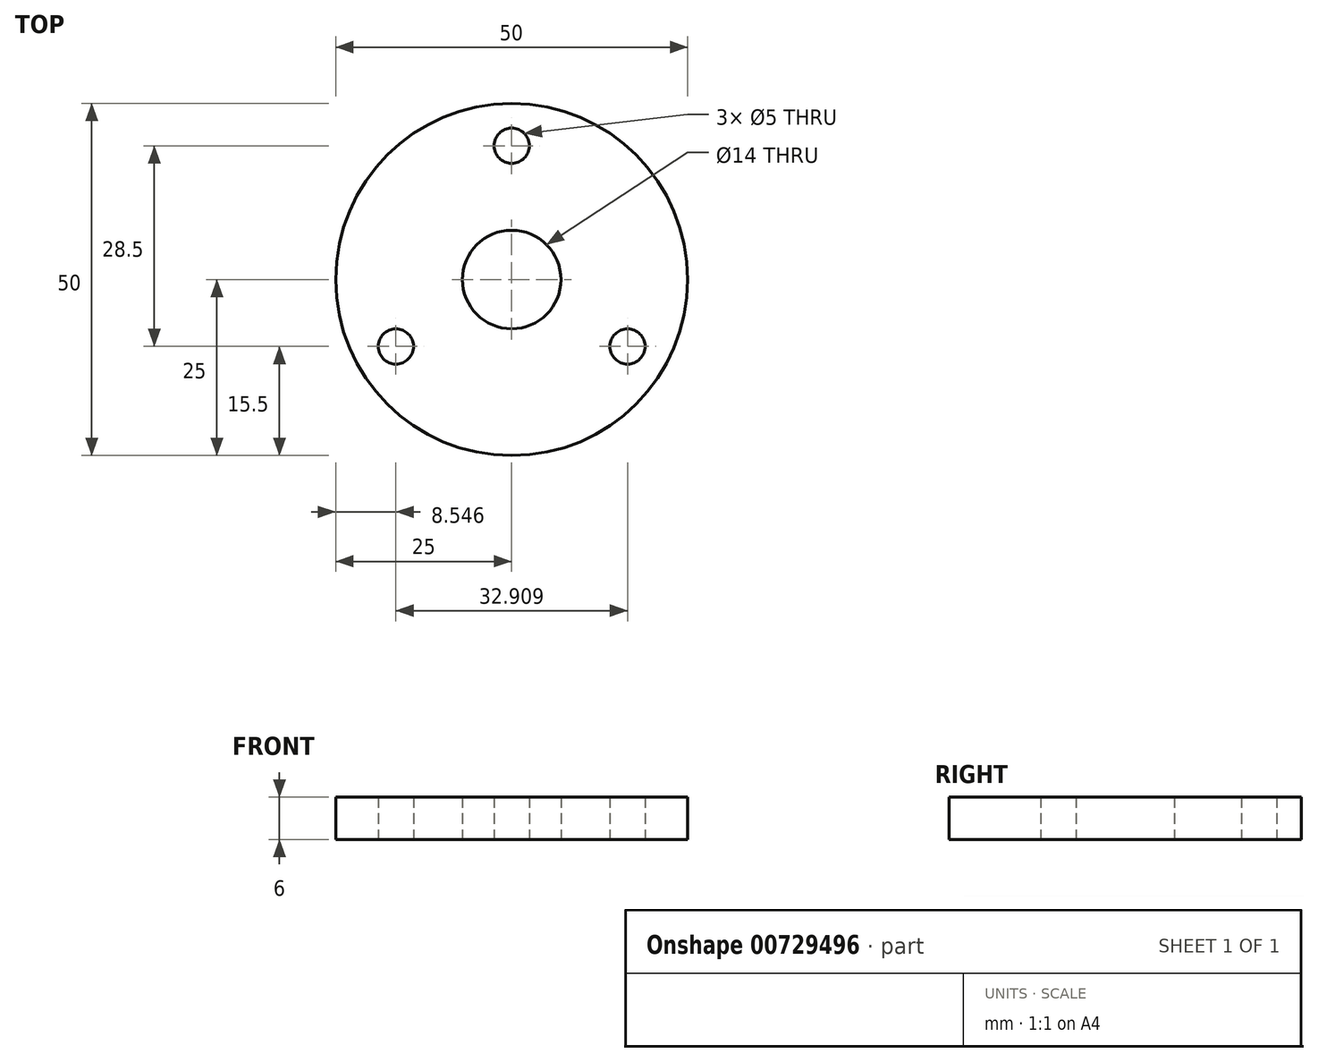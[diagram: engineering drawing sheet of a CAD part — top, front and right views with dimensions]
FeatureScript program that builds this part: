
annotation { "Feature Type Name" : "Feature", "Feature Type Description" : "" }
export const myFeature = defineFeature(function(context is Context, id is Id, definition is map)
    precondition{}
    {
        {
            var Q0;
            Q0=qCreatedBy(makeId("Top.planeOp"),FACE);
            var sketch = newSketch(context, id + "F0", { "sketchPlane" : qUnion([Q0])});
            skCircle(sketch, "E0", {"center": v(0, 0) * mm, "radius": 25 * mm});
            skCircle(sketch, "E1", {"center": v(0, 0) * mm, "radius": 7 * mm});
            skCircle(sketch, "E2", {"center": v(0, 19) * mm, "radius": 2.5 * mm});
            skCircle(sketch, "E3", {"center": v(-16.45, -9.5) * mm, "radius": 2.5 * mm});
            skCircle(sketch, "E4", {"center": v(16.45, -9.5) * mm, "radius": 2.5 * mm});
            skLineSegment(sketch, "E5", {"start": v(0, 0) * mm, "end": v(-16.45, -9.5) * mm, "construction": true});
            skLineSegment(sketch, "E6", {"start": v(0, 0) * mm, "end": v(16.45, -9.5) * mm, "construction": true});
            skSolve(sketch);
        }
        {
            var Q0;
            Q0=makeQuery(id+"F0.imprint","IMPRINT",FACE,{"disambiguationData":[TD([[makeQuery(id+"F0.imprint","IMPRINT",EDGE,{"derivedFrom":sQuery(id+"F0.wireOp",EDGE,"E0")}),1.0]])]});
            extrude(context, id + "F1", {"entities" : qUnion([Q0]), "depth" : 6 * mm, "offsetDistance" : 25 * mm});
        }
    });
